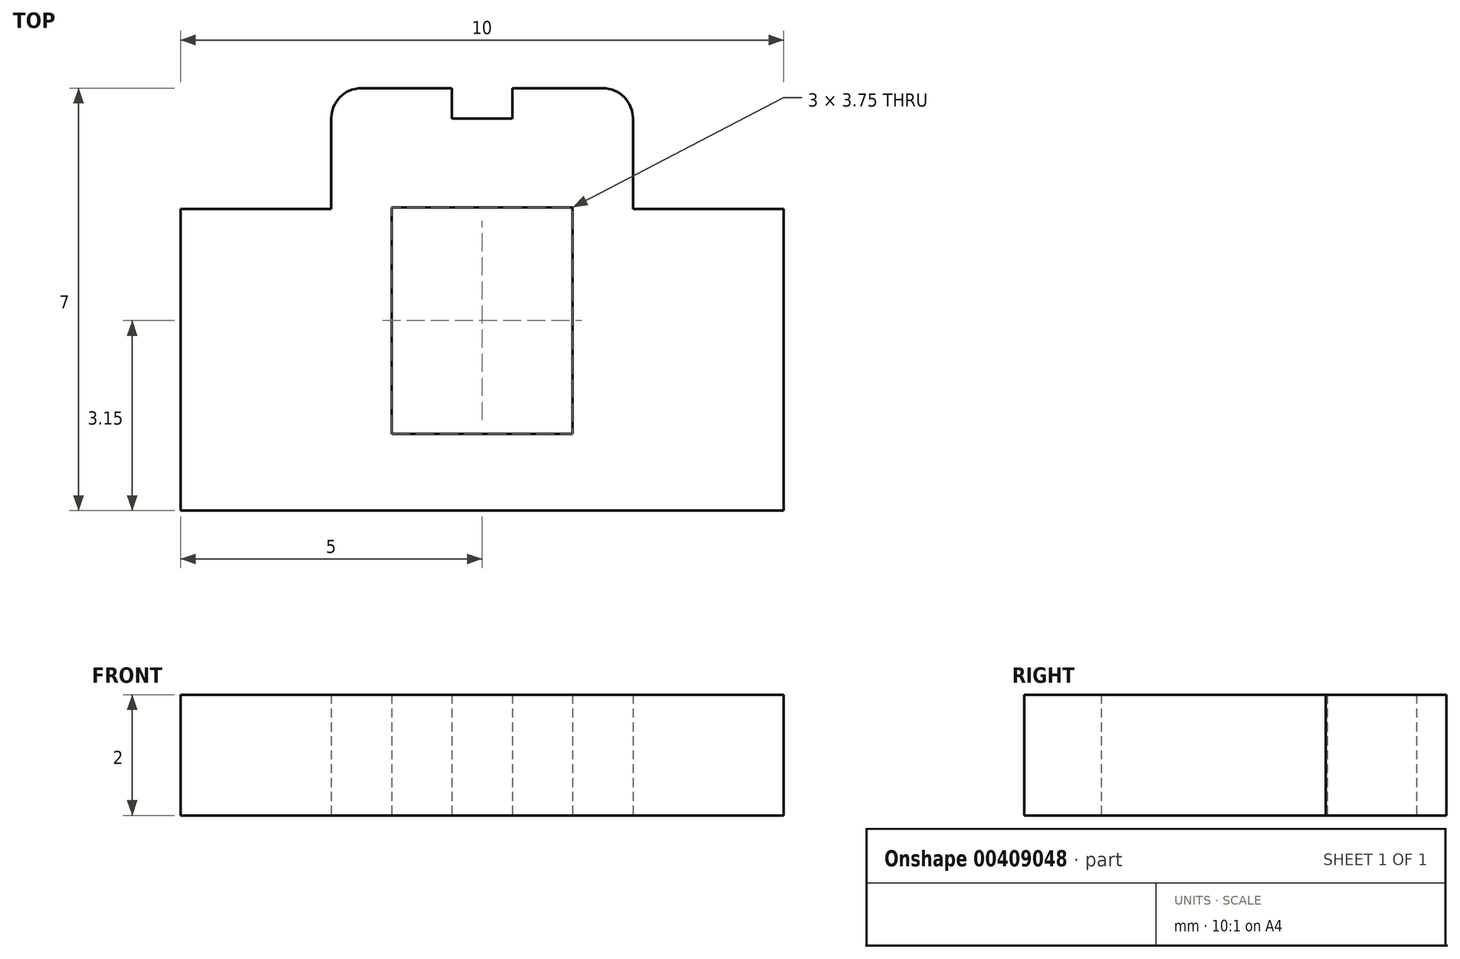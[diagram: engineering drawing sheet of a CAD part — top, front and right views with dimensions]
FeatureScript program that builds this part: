
annotation { "Feature Type Name" : "Feature", "Feature Type Description" : "" }
export const myFeature = defineFeature(function(context is Context, id is Id, definition is map)
    precondition{}
    {
        {
            var Q0;
            Q0=qCreatedBy(makeId("Top.planeOp"),FACE);
            var sketch = newSketch(context, id + "F0", { "sketchPlane" : qUnion([Q0])});
            skLineSegment(sketch, "E0.bottom", {"start": v(1.5, -1.87) * mm, "end": v(-1.5, -1.88) * mm});
            skLineSegment(sketch, "E0.top", {"start": v(1.5, 1.88) * mm, "end": v(-1.5, 1.88) * mm});
            skLineSegment(sketch, "E0.left", {"start": v(1.5, -1.88) * mm, "end": v(1.5, 1.88) * mm});
            skLineSegment(sketch, "E0.right", {"start": v(-1.5, -1.88) * mm, "end": v(-1.5, 1.88) * mm});
            skPoint(sketch, "E0.middle", {"position": v(0, 0) * mm});
            skLineSegment(sketch, "E1.bottom", {"start": v(-5, 1.85) * mm, "end": v(5, 1.85) * mm});
            skLineSegment(sketch, "E1.top", {"start": v(-5, -3.15) * mm, "end": v(5, -3.15) * mm});
            skLineSegment(sketch, "E1.left", {"start": v(-5, 1.85) * mm, "end": v(-5, -3.15) * mm});
            skLineSegment(sketch, "E1.right", {"start": v(5, 1.85) * mm, "end": v(5, -3.15) * mm});
            skLineSegment(sketch, "E2.bottom", {"start": v(-2.5, 1.85) * mm, "end": v(2.5, 1.85) * mm});
            skLineSegment(sketch, "E2.top", {"start": v(-2.5, 3.85) * mm, "end": v(2.5, 3.85) * mm});
            skLineSegment(sketch, "E2.left", {"start": v(-2.5, 1.85) * mm, "end": v(-2.5, 3.85) * mm});
            skLineSegment(sketch, "E2.right", {"start": v(2.5, 1.85) * mm, "end": v(2.5, 3.85) * mm});
            skLineSegment(sketch, "E3.bottom", {"start": v(0.5, 3.35) * mm, "end": v(-0.5, 3.35) * mm});
            skLineSegment(sketch, "E3.top", {"start": v(0.5, 4.35) * mm, "end": v(-0.5, 4.35) * mm});
            skLineSegment(sketch, "E3.left", {"start": v(0.5, 3.35) * mm, "end": v(0.5, 4.35) * mm});
            skLineSegment(sketch, "E3.right", {"start": v(-0.5, 3.35) * mm, "end": v(-0.5, 4.35) * mm});
            skPoint(sketch, "E3.middle", {"position": v(0, 3.85) * mm});
            skSolve(sketch);
        }
        {
            var Q0;
            {var subQ0=sQuery(id+"F0.wireOp",EDGE,"E2.left");Q0=makeQuery(id+"F0.imprint","IMPRINT",FACE,{"disambiguationData":[TD([[makeQuery(id+"F0.imprint","IMPRINT",EDGE,{"derivedFrom":subQ0}),-1.0]])]});}
            var Q1;
            Q1=makeQuery(id+"F0.imprint","IMPRINT",FACE,{"disambiguationData":[TD([[makeQuery(id+"F0.imprint","IMPRINT",EDGE,{"derivedFrom":sQuery(id+"F0.wireOp",EDGE,"E0.bottom")}),1.0]])]});
            extrude(context, id + "F1", {"entities" : qUnion([Q0, Q1]), "depth" : 2 * mm});
        }
        {
            var Q0;
            Q0=makeQuery(id+"F1.opExtrude","SWEPT_EDGE",EDGE,{"disambiguationData":[OSD([sQuery(id+"F0.wireOp",EDGE,"E2.top"),sQuery(id+"F0.wireOp",EDGE,"E2.left")])]});
            var Q1;
            Q1=makeQuery(id+"F1.opExtrude","SWEPT_EDGE",EDGE,{"disambiguationData":[OSD([sQuery(id+"F0.wireOp",EDGE,"E2.top"),sQuery(id+"F0.wireOp",EDGE,"E2.right")])]});
            fillet(context, id + "F2", {"entities" : qUnion([Q0, Q1]), "radius" : 0.5 * mm, "tangentPropagation" : true, "allowEdgeOverflow" : false});
        }
    });
